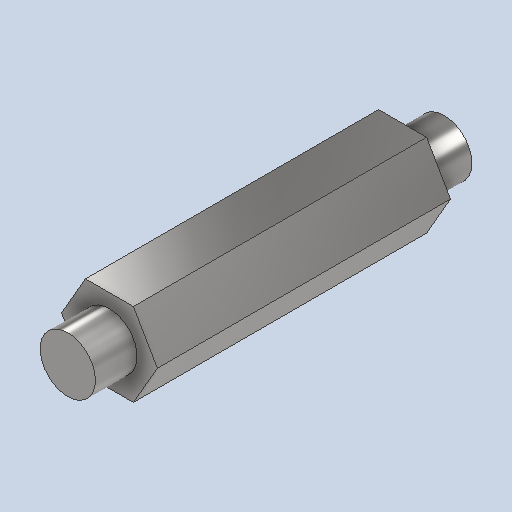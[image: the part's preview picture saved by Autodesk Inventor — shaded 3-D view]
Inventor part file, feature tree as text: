
AUTODESK INVENTOR PART (.ipt)
format: ipt  version: 2025.1 (Build 291241020, 241B)  size: 134,656 bytes
history: native  units: in
note: dims shown in document units (in); Inventor stores cm internally (conversion verified against a paired STEP export)
features: extrude x2
ambient origin geometry x8: Origin, YZ Plane, XZ Plane, XY Plane, X Axis, Y Axis, Z Axis, Center Point
bodies: Solid1 (feature_tree)
feature tree (2):
  extrude  "Extrusion1"  Depth=0.25in
  extrude  "Extrusion2"  Depth=1.7in TaperAngle=0.0deg
